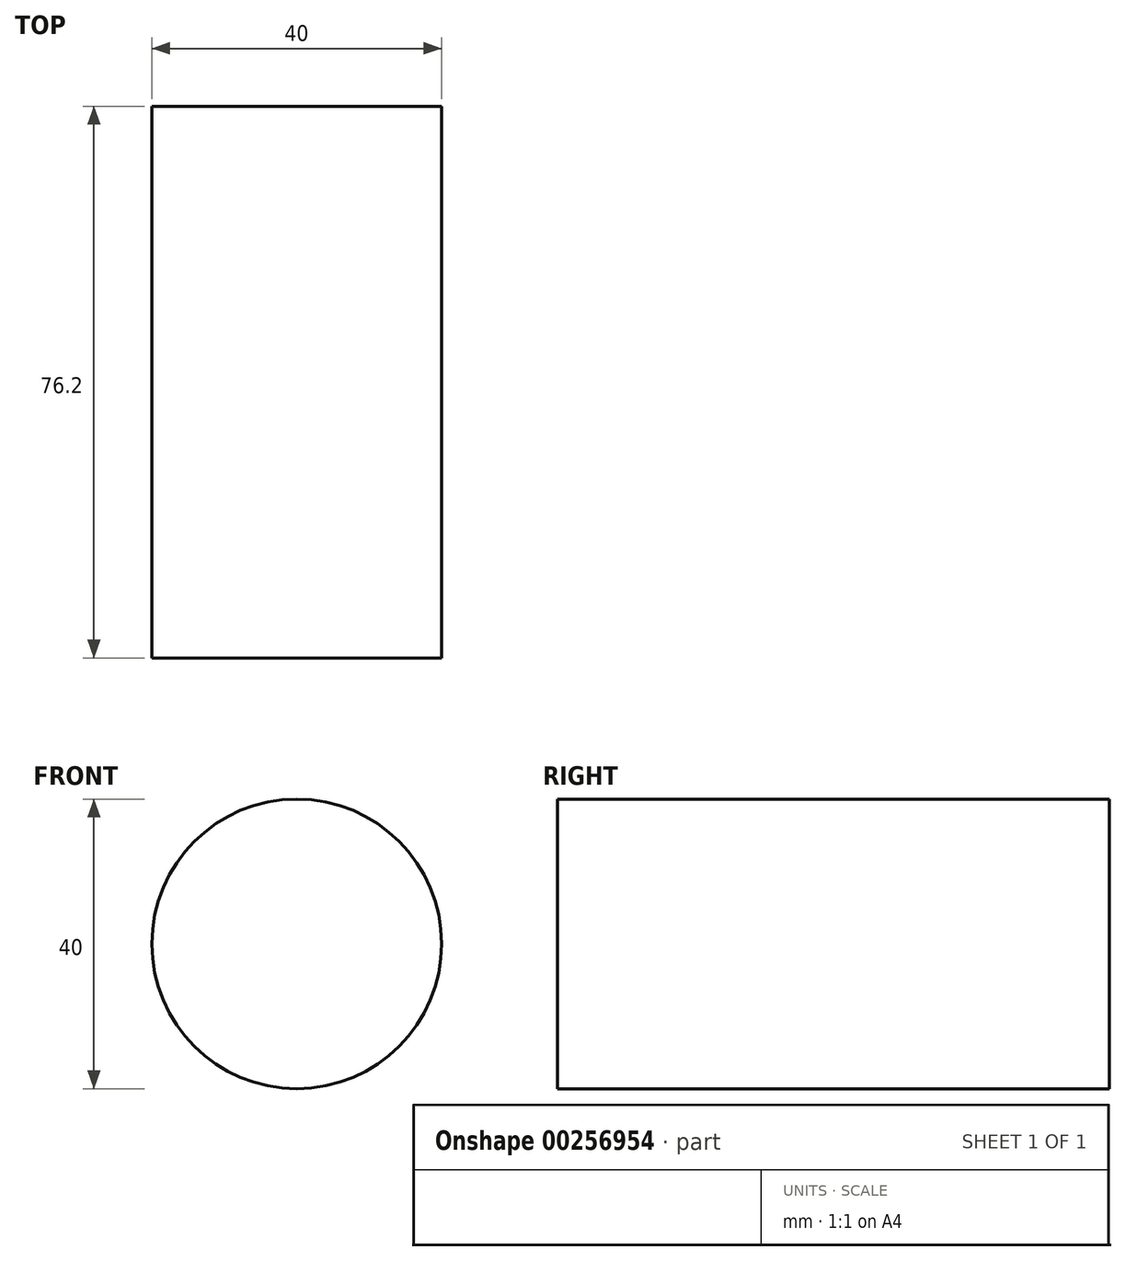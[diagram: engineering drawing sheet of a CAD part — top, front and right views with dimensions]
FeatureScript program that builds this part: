
annotation { "Feature Type Name" : "Feature", "Feature Type Description" : "" }
export const myFeature = defineFeature(function(context is Context, id is Id, definition is map)
    precondition{}
    {
        {
            var Q0;
            Q0=qCreatedBy(makeId("Front.planeOp"),FACE);
            var sketch = newSketch(context, id + "F0", { "sketchPlane" : qUnion([Q0])});
            skCircle(sketch, "E0", {"center": v(0, 0) * mm, "radius": 20 * mm});
            skSolve(sketch);
        }
        {
            var Q0;
            Q0=makeQuery(id+"F0.imprint","IMPRINT",FACE,{"disambiguationData":[TD([[makeQuery(id+"F0.imprint","IMPRINT",EDGE,{"derivedFrom":sQuery(id+"F0.wireOp",EDGE,"E0")}),1.0]])]});
            extrude(context, id + "F1", {"entities" : qUnion([Q0]), "depth" : 76.2 * mm});
        }
    });
